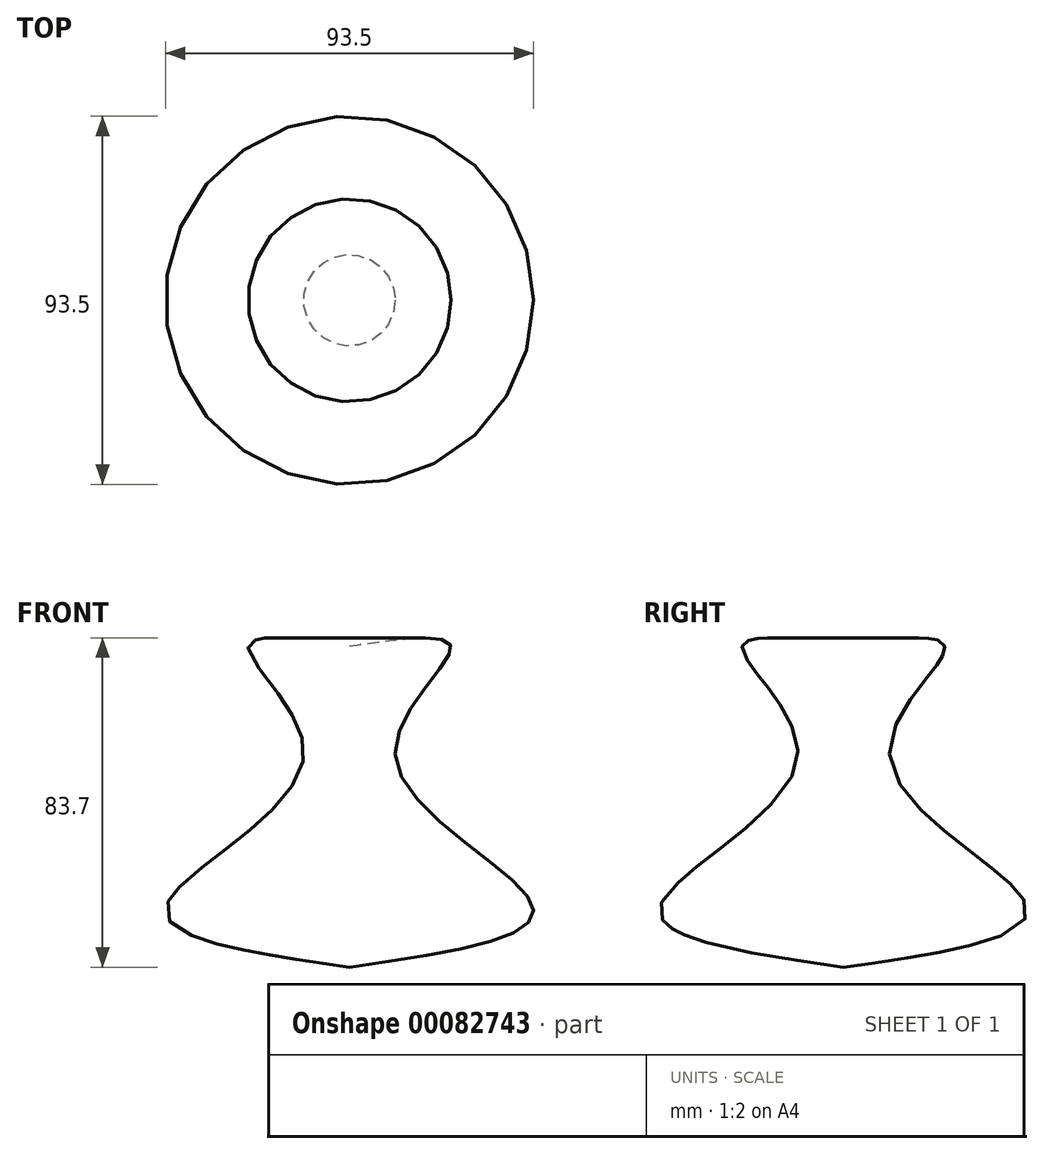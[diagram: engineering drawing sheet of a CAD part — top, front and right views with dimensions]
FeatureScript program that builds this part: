
annotation { "Feature Type Name" : "Feature", "Feature Type Description" : "" }
export const myFeature = defineFeature(function(context is Context, id is Id, definition is map)
    precondition{}
    {
        {
            var Q0;
            Q0=qCreatedBy(makeId("Front.planeOp"),FACE);
            var sketch = newSketch(context, id + "F0", { "sketchPlane" : qUnion([Q0])});
            skFitSpline(sketch, "E0", {"points": [v(0, 42.22) * mm, v(25.8, 41.72) * mm, v(11.73, 13.44) * mm, v(46.6, -23.96) * mm, v(0, -39.43) * mm], "startDerivative": vector(189.3, 27.11) * mm, "endDerivative": vector(-260.48, -36.94) * mm});
            skLineSegment(sketch, "E1", {"start": v(0, 42.22) * mm, "end": v(0, -39.43) * mm});
            skSolve(sketch);
        }
        {
            var Q0;
            Q0=makeQuery(id+"F0.imprint","IMPRINT",FACE,{"disambiguationData":[TD([[makeQuery(id+"F0.imprint","IMPRINT",EDGE,{"derivedFrom":sQuery(id+"F0.wireOp",EDGE,"E0")}),-1.0]])]});
            var Q1;
            Q1=sQuery(id+"F0.wireOp",EDGE,"E1");
            revolve(context, id + "F1", {"entities" : qUnion([Q0]), "axis" : qUnion([Q1]), "revolveType" : RevolveType.FULL});
        }
    });
